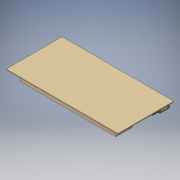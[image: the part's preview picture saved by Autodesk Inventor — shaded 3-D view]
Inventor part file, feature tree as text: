
AUTODESK INVENTOR PART (.ipt)
format: ipt  version: 2018 (Build 220112000, 112)  size: 231,424 bytes
history: native  units: in
note: dims shown in document units (in); Inventor stores cm internally (conversion verified against a paired STEP export)
features: sketch x9, extrude x8, pattern_linear x1
ambient origin geometry x8: Origin, YZ Plane, XZ Plane, XY Plane, X Axis, Y Axis, Z Axis, Center Point
bodies: Solid1 (feature_tree)
feature tree (18):
  extrude  "Extrusion1"  Depth=120.0in
  pattern_linear  "Rectangular Pattern1"  Count1=6 Spacing1=240.0in
  extrude  "Extrusion4"  Depth=100.0in TaperAngle=0.0deg
  sketch  "Sketch5"  dims[d26=100.0in d27=0.0in d28=100.0in d29=0.0in]
  extrude  "Extrusion5"  Depth=200.0in TaperAngle=0.0deg
  extrude  "Extrusion6"  Depth=50.0in TaperAngle=0.0deg
  extrude  "Extrusion7"  [1 undecoded]
  extrude  "Extrusion8"  [1 undecoded]
  extrude  "Extrusion9"  [1 undecoded]
  extrude  "Extrusion10"  [1 undecoded]
  sketch  "Sketch11"
  sketch  "Sketch1"  dims[d0=240.0in d1=120.0in]
  sketch  "Sketch4"  dims[d2=10.0in d3=0.0in d4=2.3622in d6=240.0in d7=2.3622in d9=120.0in]
  sketch  "Sketch6"  dims[d30=200.0in d31=0.0in d32=200.0in d33=0.0in]
  sketch  "Sketch7"  dims[d34=50.0in d35=0.0in d36=50.0in d37=0.0in]
  sketch  "Sketch8"  dims[d38=50.0in d39=0.0in]
  sketch  "Sketch9"
  sketch  "Sketch10"
note: 4 required parameter values undecoded (feature->parameter linkage not recoverable at this tier; creation-order binding heuristic only, values carry confidence <= 0.55)
